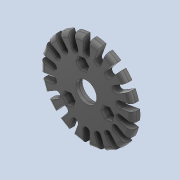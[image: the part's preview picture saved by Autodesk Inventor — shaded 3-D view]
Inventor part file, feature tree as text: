
AUTODESK INVENTOR PART (.ipt)
format: ipt  version: 2020.4 (Build 244396000, 396)  size: 409,088 bytes
history: native  units: mm
features: sketch x6, extrude x4, hole x2, fillet x1
ambient origin geometry x8: Origin, YZ Plane, XZ Plane, XY Plane, X Axis, Y Axis, Z Axis, Center Point
bodies: Solid1 (feature_tree)
feature tree (13):
  extrude  "PartB Base"  Depth=3.5mm TaperAngle=0.0deg
  extrude  "Roller Entrance"  Depth=3.2mm
  hole  "Bearing Fit"  [1 undecoded]
  extrude  "Threads Fit"  Depth=10.0mm TaperAngle=0.0deg
  extrude  "Extrusion4"  Depth=2.0mm
  hole  "Thread Fit"  [1 undecoded]
  fillet  "Ground Round"  Radius=30.0mm
  sketch  "Sketch1"  dims[d0=45.0mm d1=3.5mm d2=0.0mm]
  sketch  "Sketch2"  dims[d3=6.7mm d4=3.2mm]
  sketch  "Sketch3"  dims[d5=0.0mm d6=19.6mm]
  sketch  "Sketch4"  dims[d7=180.0mm d9=360.0deg d11=10.0mm d12=0.0mm]
  sketch  "Sketch5"  dims[d13=11.0mm d14=6.0mm d15=4.0mm d16=2.0mm d17=90.0deg d18=2.0mm d19=0.0mm d20=3.0mm]
  sketch  "Sketch6"  dims[d21=1.91013mm d22=10.833mm d23=30.0mm d25=360.0deg d27=10.0mm d28=0.0mm d29=2.76mm d30=2.76mm d31=2.76mm d32=2.75mm d33=0.0mm d34=10.0mm d35=6.0mm d36=4.0mm d37=2.0mm d38=90.0deg d39=1.5mm d40=0.0mm d41=2.0mm]
note: 2 required parameter values undecoded (feature->parameter linkage not recoverable at this tier; creation-order binding heuristic only, values carry confidence <= 0.55)
